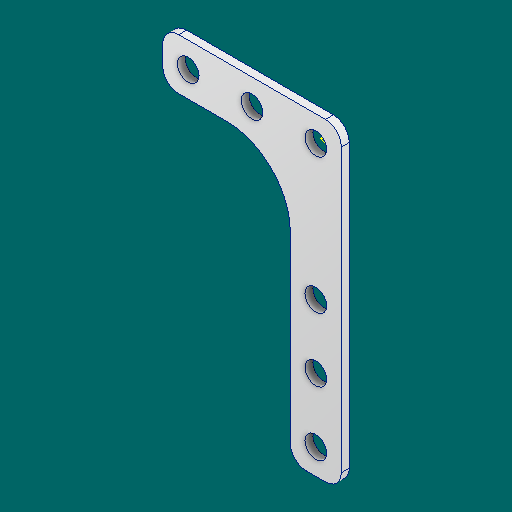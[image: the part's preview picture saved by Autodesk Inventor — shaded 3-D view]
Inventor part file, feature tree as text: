
AUTODESK INVENTOR PART (.ipt)
format: ipt  version: 2023.1 (Build 271208000, 208)  size: 136,192 bytes
history: native  units: in
note: dims shown in document units (in); Inventor stores cm internally (conversion verified against a paired STEP export)
features: fillet x2, extrude x1, sketch x1
ambient origin geometry x8: Origin, YZ Plane, XZ Plane, XY Plane, X Axis, Y Axis, Z Axis, Center Point
bodies: Solid1 (feature_tree)
feature tree (4):
  extrude  "Extrusion1"  Depth=0.0625in TaperAngle=0.0deg
  fillet  "Fillet1"  Radius=1.0607in
  fillet  "Fillet2"  Radius=0.17in
  sketch  "Sketch1"  dims[d3=1.1811in d5=0.5in d6=0.3937in d8=1.0in d19=0.0625in d20=0.0in d21=1.0607in d22=0.17in d23=1.1811in d25=0.5in d26=0.3937in d28=1.0in d30=0.4in d31=0.125in d32=0.5in]
